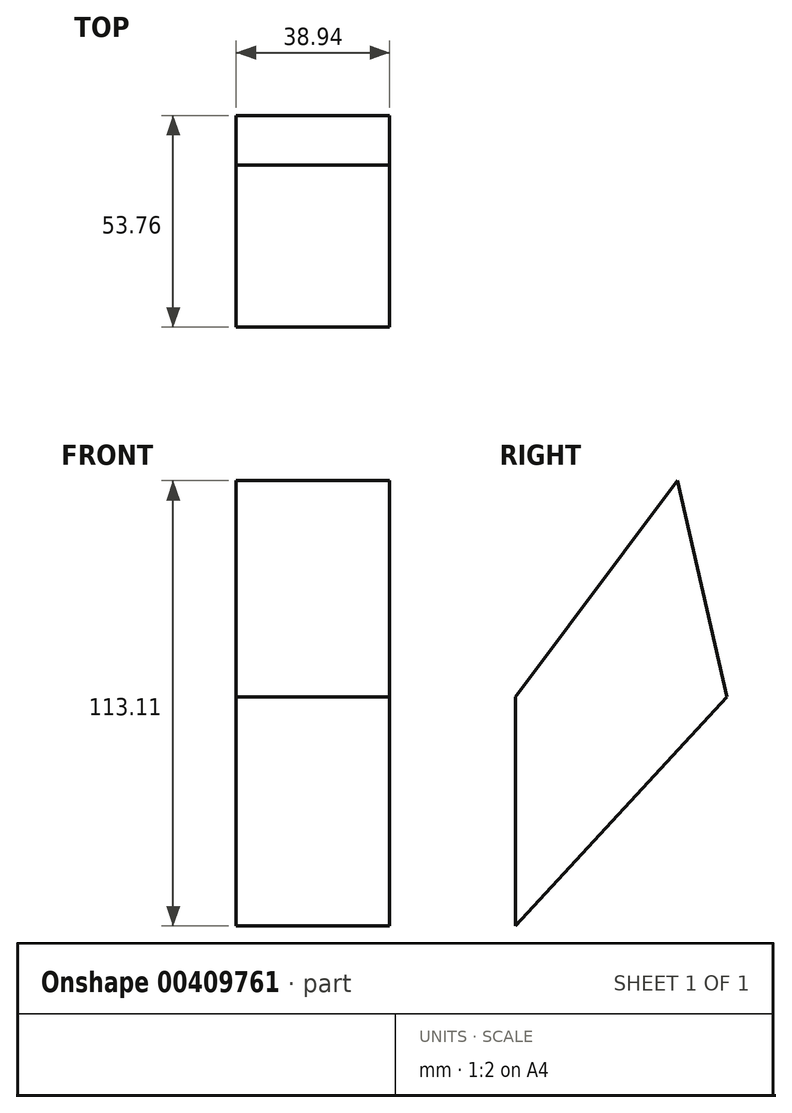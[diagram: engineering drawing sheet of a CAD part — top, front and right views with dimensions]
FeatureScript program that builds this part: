
annotation { "Feature Type Name" : "Feature", "Feature Type Description" : "" }
export const myFeature = defineFeature(function(context is Context, id is Id, definition is map)
    precondition{}
    {
        {
            var Q0;
            Q0=qCreatedBy(makeId("Right.planeOp"),FACE);
            var sketch = newSketch(context, id + "F0", { "sketchPlane" : qUnion([Q0])});
            skLineSegment(sketch, "E0", {"start": v(0, -58.23) * mm, "end": v(53.76, 0) * mm});
            skLineSegment(sketch, "E1", {"start": v(53.76, 0) * mm, "end": v(0, 0) * mm});
            skLineSegment(sketch, "E2", {"start": v(0, 0) * mm, "end": v(0, -58.23) * mm});
            skLineSegment(sketch, "E3", {"start": v(41.15, 54.88) * mm, "end": v(0, 0) * mm});
            skLineSegment(sketch, "E4", {"start": v(53.76, 0) * mm, "end": v(41.15, 54.88) * mm});
            skSolve(sketch);
        }
        {
            var Q0;
            Q0 = qSketchRegion(id + "F0", true);
            extrude(context, id + "F1", {"entities" : qUnion([Q0]), "depth" : 38.94 * mm});
        }
    });
